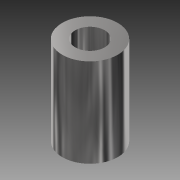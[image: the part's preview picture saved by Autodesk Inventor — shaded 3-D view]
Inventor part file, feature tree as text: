
AUTODESK INVENTOR PART (.ipt)
format: ipt  version: 2013 (Build 170138000, 138)  size: 94,720 bytes
history: native  units: mm
features: extrude x1, sketch x1
ambient origin geometry x8: Origin, YZ Plane, XZ Plane, XY Plane, X Axis, Y Axis, Z Axis, Center Point
bodies: Solid1 (feature_tree)
feature tree (2):
  extrude  "Extrusion1"  Depth=15.0mm
  sketch  "Sketch1"  dims[d0=8.0mm d2=15.0mm d3=24.0mm d4=0.0mm]
